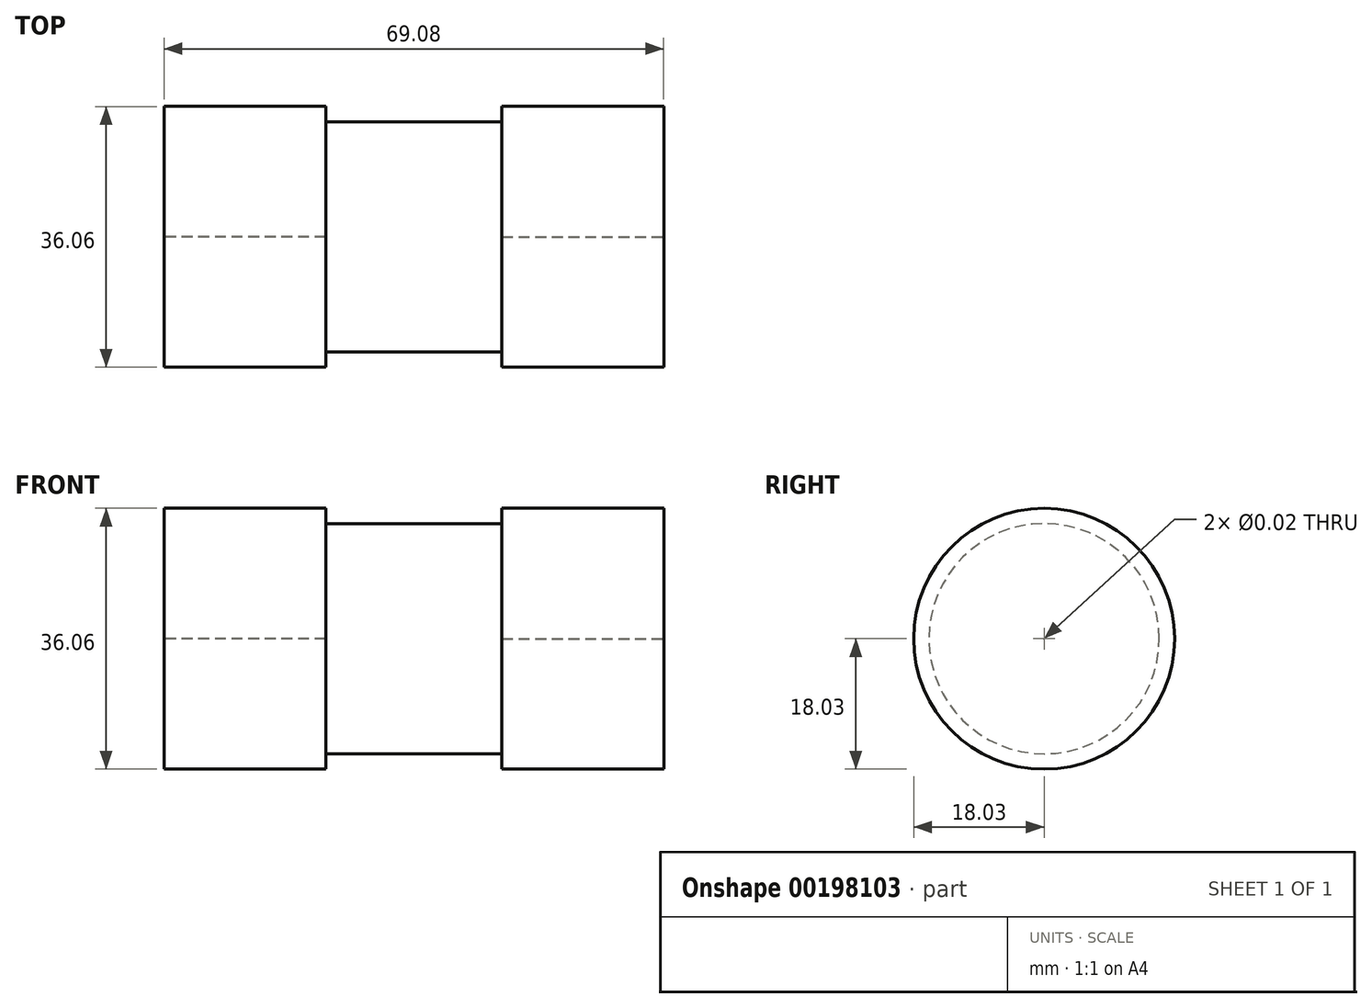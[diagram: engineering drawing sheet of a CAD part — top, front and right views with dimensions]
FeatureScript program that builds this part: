
annotation { "Feature Type Name" : "Feature", "Feature Type Description" : "" }
export const myFeature = defineFeature(function(context is Context, id is Id, definition is map)
    precondition{}
    {
        {
            var Q0;
            Q0=qCreatedBy(makeId("Right.planeOp"),FACE);
            var sketch = newSketch(context, id + "F0", { "sketchPlane" : qUnion([Q0])});
            skCircle(sketch, "E0", {"center": v(0, 0) * mm, "radius": 18.03 * mm});
            skSolve(sketch);
        }
        {
            var Q0;
            Q0 = qSketchRegion(id + "F0", true);
            extrude(context, id + "F1", {"entities" : qUnion([Q0]), "endBound" : BoundingType.SYMMETRIC, "depth" : 69.1 * mm});
        }
        {
            var Q0;
            Q0=qCreatedBy(makeId("Front.planeOp"),FACE);
            var sketch = newSketch(context, id + "F2", { "sketchPlane" : qUnion([Q0])});
            skLineSegment(sketch, "E1", {"start": v(-88.1, 0) * mm, "end": v(100.19, 0) * mm, "construction": true});
            skLineSegment(sketch, "E2.0", {"start": v(-34.54, 18.03) * mm, "end": v(-34.54, -18.03) * mm, "construction": true});
            skLineSegment(sketch, "E3.0", {"start": v(34.54, 18.03) * mm, "end": v(34.54, -18.03) * mm, "construction": true});
            skLineSegment(sketch, "E4.0", {"start": v(12.2, 18.03) * mm, "end": v(12.2, -18.03) * mm, "construction": true});
            skLineSegment(sketch, "E5.0", {"start": v(-12.2, 18.2) * mm, "end": v(-12.2, -18.03) * mm, "construction": true});
            skLineSegment(sketch, "E6.bottom", {"start": v(-12.2, 18.2) * mm, "end": v(12.2, 18.2) * mm});
            skLineSegment(sketch, "E6.top", {"start": v(-12.2, 15.92) * mm, "end": v(12.2, 15.92) * mm});
            skLineSegment(sketch, "E6.left", {"start": v(-12.2, 18.2) * mm, "end": v(-12.2, 15.92) * mm});
            skLineSegment(sketch, "E6.right", {"start": v(12.2, 18.2) * mm, "end": v(12.2, 15.92) * mm});
            skSolve(sketch);
        }
        {
            var Q0;
            Q0=makeQuery(id+"F2.imprint","IMPRINT",FACE,{"disambiguationData":[TD([[makeQuery(id+"F2.imprint","IMPRINT",EDGE,{"derivedFrom":sQuery(id+"F2.wireOp",EDGE,"E6.bottom")}),-1.0]])]});
            var Q1;
            Q1=sQuery(id+"F2.wireOp",EDGE,"E1");
            revolve(context, id + "F3", {"operationType" : NewBodyOperationType.REMOVE, "entities" : qUnion([Q0]), "axis" : qUnion([Q1]), "revolveType" : RevolveType.FULL, "oppositeDirection" : true});
        }
        {
            var Q0;
            Q0=makeQuery(id+"F1.opExtrude","CAP_FACE",FACE,{"disambiguationData":[OSD([sQuery(id+"F0.wireOp",EDGE,"E0")])],"isStart":false});
            var sketch = newSketch(context, id + "F4", { "sketchPlane" : qUnion([Q0])});
            skPoint(sketch, "E7", {"position": v(0, 0) * mm});
            skSolve(sketch);
        }
        {
            var Q0;
            Q0=sQuery(id+"F4.wireOp",VERTEX,"E7");
            var Q1;
            Q1=makeQuery(id+"F1.opExtrude","SWEPT_BODY",BODY,{"disambiguationData":[OSD([sQuery(id+"F0.wireOp",EDGE,"E0")])]});
            hole(context, id + "F5", {"style" : HoleStyle.SIMPLE, "endStyle" : HoleEndStyle.BLIND, "standardTappedOrClearance" : lookupTablePath({ "standard" : "ANSI", "size" : "1/2 (0.5)", "type" : "Drilled" }), "standardBlindInLast" : lookupTablePath({ "standard" : "ANSI", "size" : "1/2", "type" : "Drilled" }), "holeDiameter" : 1 / 50.8 * mm, "holeDepth" : 22.35 * mm, "locations" : qUnion([Q0]), "scope" : qUnion([Q1])});
        }
        {
            var Q0;
            Q0=makeQuery(id+"F1.opExtrude","CAP_FACE",FACE,{"disambiguationData":[OSD([sQuery(id+"F0.wireOp",EDGE,"E0")])],"isStart":true});
            var sketch = newSketch(context, id + "F6", { "sketchPlane" : qUnion([Q0])});
            skPoint(sketch, "E8", {"position": v(0, 0) * mm});
            skSolve(sketch);
        }
        {
            var Q0;
            Q0=sQuery(id+"F6.wireOp",VERTEX,"E8");
            var Q1;
            Q1=makeQuery(id+"F1.opExtrude","SWEPT_BODY",BODY,{"disambiguationData":[OSD([sQuery(id+"F0.wireOp",EDGE,"E0")])]});
            hole(context, id + "F7", {"style" : HoleStyle.SIMPLE, "endStyle" : HoleEndStyle.BLIND, "standardTappedOrClearance" : lookupTablePath({ "standard" : "ANSI", "size" : "5/8 (0.62)", "type" : "Drilled" }), "standardBlindInLast" : lookupTablePath({ "standard" : "ANSI", "size" : "5/8", "type" : "Drilled" }), "holeDiameter" : 5 / 203.2 * mm, "holeDepth" : 22.35 * mm, "locations" : qUnion([Q0]), "scope" : qUnion([Q1])});
        }
    });
